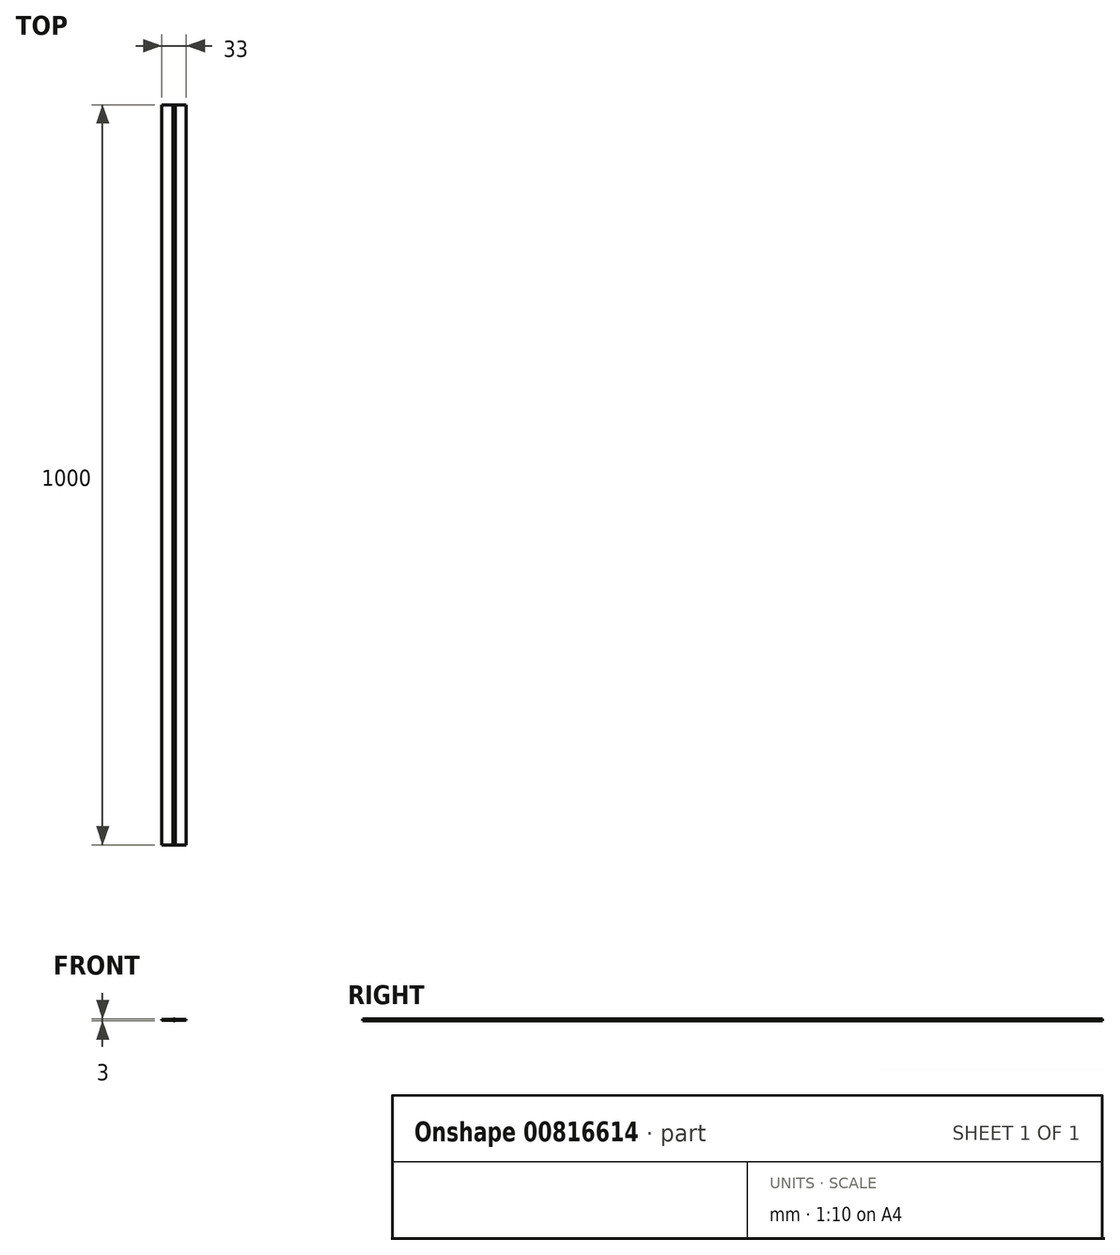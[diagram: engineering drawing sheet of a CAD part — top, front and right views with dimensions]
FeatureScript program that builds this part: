
annotation { "Feature Type Name" : "Feature", "Feature Type Description" : "" }
export const myFeature = defineFeature(function(context is Context, id is Id, definition is map)
    precondition{}
    {
        {
            var Q0;
            Q0=qCreatedBy(makeId("Front.planeOp"),FACE);
            var sketch = newSketch(context, id + "F0", { "sketchPlane" : qUnion([Q0])});
            skCircle(sketch, "E0", {"center": v(0, 0) * mm, "radius": 1.5 * mm});
            skSolve(sketch);
        }
        {
            var Q0;
            Q0 = qSketchRegion(id + "F0", true);
            extrude(context, id + "F1", {"entities" : qUnion([Q0]), "endBound" : BoundingType.SYMMETRIC, "depth" : 1000 * mm, "offsetDistance" : 25 * mm});
        }
        {
            var Q0;
            Q0=qCreatedBy(makeId("Front.planeOp"),FACE);
            var sketch = newSketch(context, id + "F2", { "sketchPlane" : qUnion([Q0])});
            skLineSegment(sketch, "E1.bottom", {"start": v(0, 0.5) * mm, "end": v(16.5, 0.5) * mm});
            skLineSegment(sketch, "E1.top", {"start": v(0, -0.5) * mm, "end": v(16.5, -0.5) * mm});
            skLineSegment(sketch, "E1.left", {"start": v(0, 0.5) * mm, "end": v(0, -0.5) * mm});
            skLineSegment(sketch, "E1.right", {"start": v(16.5, 0.5) * mm, "end": v(16.5, -0.5) * mm});
            skSolve(sketch);
        }
        {
            var Q0;
            Q0 = qSketchRegion(id + "F2", true);
            extrude(context, id + "F3", {"entities" : qUnion([Q0]), "operationType" : NewBodyOperationType.ADD, "endBound" : BoundingType.SYMMETRIC, "depth" : 1000 * mm, "offsetDistance" : 25 * mm});
        }
        {
            var Q0;
            Q0=qCreatedBy(makeId("Front.planeOp"),FACE);
            var sketch = newSketch(context, id + "F4", { "sketchPlane" : qUnion([Q0])});
            skCircle(sketch, "E2", {"center": v(0, 0) * mm, "radius": 1.5 * mm});
            skSolve(sketch);
        }
        {
            var Q0;
            Q0 = qSketchRegion(id + "F4", true);
            extrude(context, id + "F5", {"entities" : qUnion([Q0]), "endBound" : BoundingType.SYMMETRIC, "depth" : 1000 * mm, "offsetDistance" : 25 * mm});
        }
        {
            var Q0;
            Q0=qCreatedBy(makeId("Front.planeOp"),FACE);
            var sketch = newSketch(context, id + "F6", { "sketchPlane" : qUnion([Q0])});
            skLineSegment(sketch, "E3.bottom", {"start": v(-16.5, 0.5) * mm, "end": v(0, 0.5) * mm});
            skLineSegment(sketch, "E3.top", {"start": v(-16.5, -0.5) * mm, "end": v(0, -0.5) * mm});
            skLineSegment(sketch, "E3.left", {"start": v(-16.5, 0.5) * mm, "end": v(-16.5, -0.5) * mm});
            skLineSegment(sketch, "E3.right", {"start": v(0, 0.5) * mm, "end": v(0, -0.5) * mm});
            skSolve(sketch);
        }
        {
            var Q0;
            Q0 = qSketchRegion(id + "F6", true);
            extrude(context, id + "F7", {"entities" : qUnion([Q0]), "operationType" : NewBodyOperationType.ADD, "endBound" : BoundingType.SYMMETRIC, "depth" : 1000 * mm, "offsetDistance" : 25 * mm});
        }
    });
